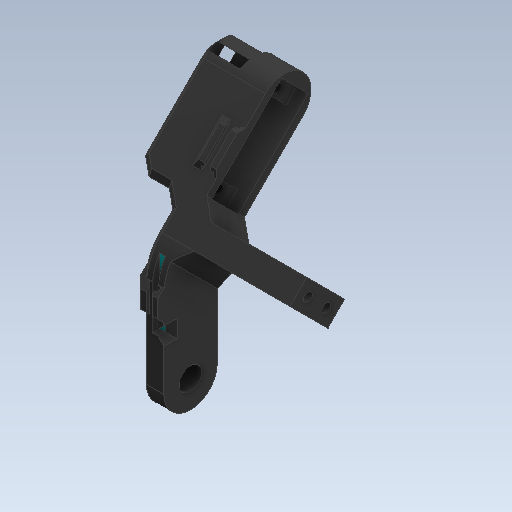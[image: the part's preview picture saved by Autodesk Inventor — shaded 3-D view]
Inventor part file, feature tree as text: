
AUTODESK INVENTOR PART (.ipt)
format: ipt  version: 2020 (Build 240168000, 168)  size: 415,232 bytes
history: native  units: in
note: dims shown in document units (in); Inventor stores cm internally (conversion verified against a paired STEP export)
features: sketch x22, other x7, plane x4
ambient origin geometry x8: Origin, YZ Plane, XZ Plane, XY Plane, X Axis, Y Axis, Z Axis, Center Point
bodies: Solid2 (feature_tree), Solid3 (feature_tree), Solid1 (feature_tree), Solid4 (feature_tree)
feature tree (33):
  other  "PatellaBot.ipt"
  other  "Solid1::PatellaBot.ipt"
  other  "Solid4::PatellaBot.ipt"
  other  "Solid5::PatellaBot.ipt"
  other  "Solid2::PatellaBot.ipt"
  other  "Solid3::PatellaBot.ipt"
  other  "TaggingFeature1"
  sketch  "Sketch1"  dims[d0=0.3937in]
  sketch  "Sketch2"
  sketch  "Sketch3"
  sketch  "Sketch4"
  sketch  "Sketch5"
  sketch  "Sketch12"
  sketch  "Sketch14"
  sketch  "Sketch15"
  sketch  "Sketch16"
  sketch  "Sketch17"
  sketch  "Sketch19"
  sketch  "Sketch22"
  sketch  "Sketch23"
  sketch  "Sketch25"
  sketch  "Sketch26"
  sketch  "Sketch27"
  sketch  "Sketch28"
  sketch  "Sketch32"
  sketch  "Sketch33"
  sketch  "Sketch39"
  sketch  "Sketch40"
  sketch  "Sketch46"
  plane  "Work Plane1"
  plane  "Work Plane2"
  plane  "Work Plane3"
  plane  "Work Plane4"
